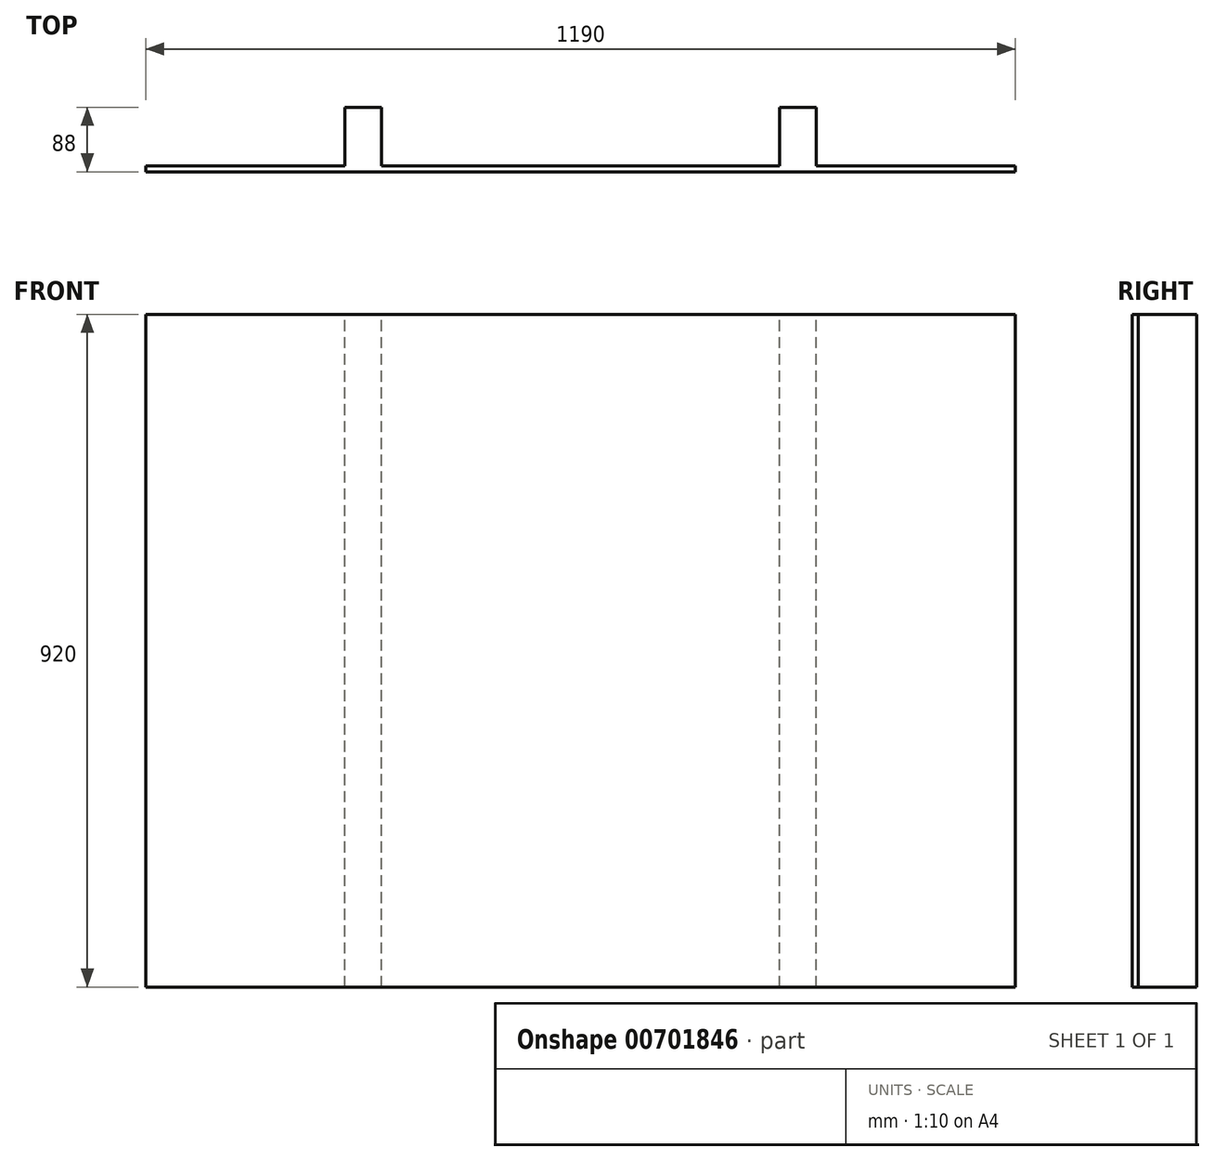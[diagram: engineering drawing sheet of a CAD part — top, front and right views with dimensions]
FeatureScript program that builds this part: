
annotation { "Feature Type Name" : "Feature", "Feature Type Description" : "" }
export const myFeature = defineFeature(function(context is Context, id is Id, definition is map)
    precondition{}
    {
        {
            var Q0;
            Q0=qCreatedBy(makeId("Front.planeOp"),FACE);
            var sketch = newSketch(context, id + "F0", { "sketchPlane" : qUnion([Q0])});
            skLineSegment(sketch, "E0.bottom", {"start": v(0, 0) * mm, "end": v(1190, 0) * mm});
            skLineSegment(sketch, "E0.top", {"start": v(0, 920) * mm, "end": v(1190, 920) * mm});
            skLineSegment(sketch, "E0.left", {"start": v(0, 0) * mm, "end": v(0, 920) * mm});
            skLineSegment(sketch, "E0.right", {"start": v(1190, 0) * mm, "end": v(1190, 920) * mm});
            skSolve(sketch);
        }
        {
            var Q0;
            Q0=makeQuery(id+"F0.imprint","IMPRINT",FACE,{"disambiguationData":[TD([[makeQuery(id+"F0.imprint","IMPRINT",EDGE,{"derivedFrom":sQuery(id+"F0.wireOp",EDGE,"E0.bottom")}),1.0]])]});
            extrude(context, id + "F1", {"entities" : qUnion([Q0]), "depth" : 8 * mm, "offsetDistance" : 25 * mm});
        }
        {
            var Q0;
            Q0=makeQuery(id+"F1.opExtrude","CAP_FACE",FACE,{"disambiguationData":[OSD([sQuery(id+"F0.wireOp",EDGE,"E0.bottom"),sQuery(id+"F0.wireOp",EDGE,"E0.top"),sQuery(id+"F0.wireOp",EDGE,"E0.left"),sQuery(id+"F0.wireOp",EDGE,"E0.right")])],"isStart":true});
            var sketch = newSketch(context, id + "F2", { "sketchPlane" : qUnion([Q0])});
            skLineSegment(sketch, "E1", {"start": v(-595, 920) * mm, "end": v(-595, 0) * mm, "construction": true});
            skLineSegment(sketch, "E2.bottom", {"start": v(-272.5, 0) * mm, "end": v(-322.5, 0) * mm});
            skLineSegment(sketch, "E2.top", {"start": v(-272.5, 920) * mm, "end": v(-322.5, 920) * mm});
            skLineSegment(sketch, "E2.left", {"start": v(-272.5, 0) * mm, "end": v(-272.5, 920) * mm});
            skLineSegment(sketch, "E2.right", {"start": v(-322.5, 0) * mm, "end": v(-322.5, 920) * mm});
            skPoint(sketch, "E2.middle", {"position": v(-297.5, 460) * mm});
            skPoint(sketch, "E2.middle.positionSnap0", {"position": v(-595, 460) * mm});
            skPoint(sketch, "E2.centerSnap0", {"position": v(-595, 460) * mm});
            skLineSegment(sketch, "E3.MirrorCS", {"start": v(-867.5, 0) * mm, "end": v(-867.5, 920) * mm});
            skLineSegment(sketch, "E4.MirrorCS", {"start": v(-917.5, 920) * mm, "end": v(-867.5, 920) * mm});
            skLineSegment(sketch, "E5.MirrorCS", {"start": v(-917.5, 0) * mm, "end": v(-917.5, 920) * mm});
            skLineSegment(sketch, "E6.MirrorCS", {"start": v(-917.5, 0) * mm, "end": v(-867.5, 0) * mm});
            skSolve(sketch);
        }
        {
            var Q0;
            Q0=makeQuery(id+"F2.imprint","IMPRINT",FACE,{"disambiguationData":[TD([[makeQuery(id+"F2.imprint","IMPRINT",EDGE,{"derivedFrom":sQuery(id+"F2.wireOp",EDGE,"E3.MirrorCS")}),1.0]])]});
            var Q1;
            Q1=makeQuery(id+"F2.imprint","IMPRINT",FACE,{"disambiguationData":[TD([[makeQuery(id+"F2.imprint","IMPRINT",EDGE,{"derivedFrom":sQuery(id+"F2.wireOp",EDGE,"E2.bottom")}),-1.0]])]});
            extrude(context, id + "F3", {"entities" : qUnion([Q0, Q1]), "operationType" : NewBodyOperationType.ADD, "depth" : 80 * mm, "offsetDistance" : 25 * mm});
        }
    });
